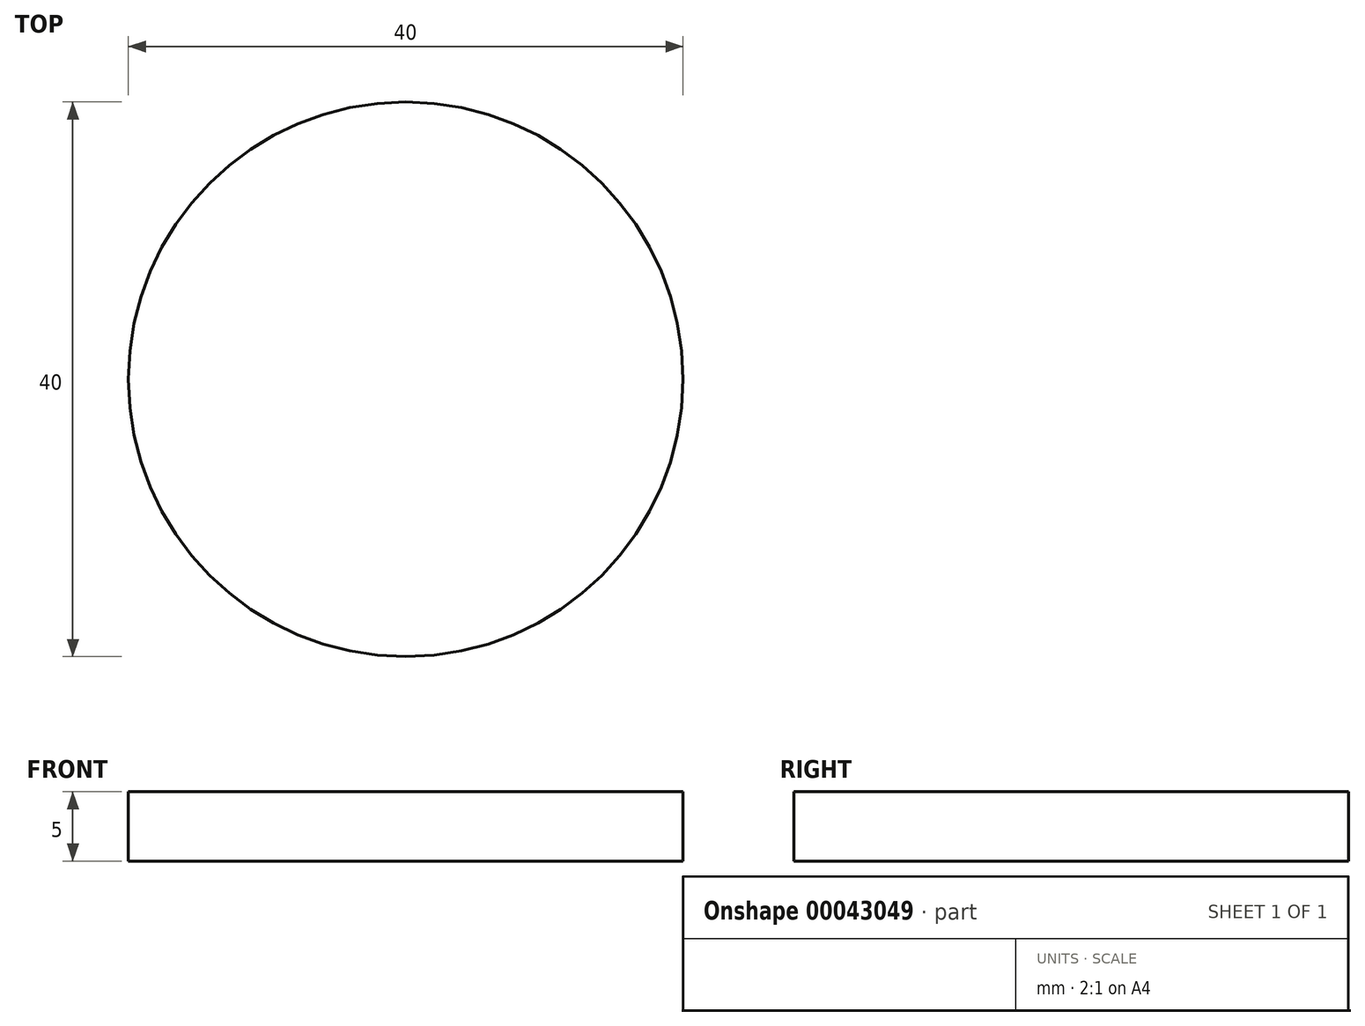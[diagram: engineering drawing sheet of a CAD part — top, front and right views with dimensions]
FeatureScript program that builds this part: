
annotation { "Feature Type Name" : "Feature", "Feature Type Description" : "" }
export const myFeature = defineFeature(function(context is Context, id is Id, definition is map)
    precondition{}
    {
        {
            var Q0;
            Q0=qCreatedBy(makeId("Top.planeOp"),FACE);
            var sketch = newSketch(context, id + "F0", { "sketchPlane" : qUnion([Q0])});
            skCircle(sketch, "E0", {"center": v(0, 0) * mm, "radius": 20 * mm});
            skSolve(sketch);
        }
        {
            var Q0;
            Q0=makeQuery(id+"F0.imprint","IMPRINT",FACE,{"disambiguationData":[TD([[makeQuery(id+"F0.imprint","IMPRINT",EDGE,{"derivedFrom":sQuery(id+"F0.wireOp",EDGE,"E0")}),1.0]])]});
            extrude(context, id + "F1", {"entities" : qUnion([Q0]), "depth" : 5 * mm});
        }
    });
